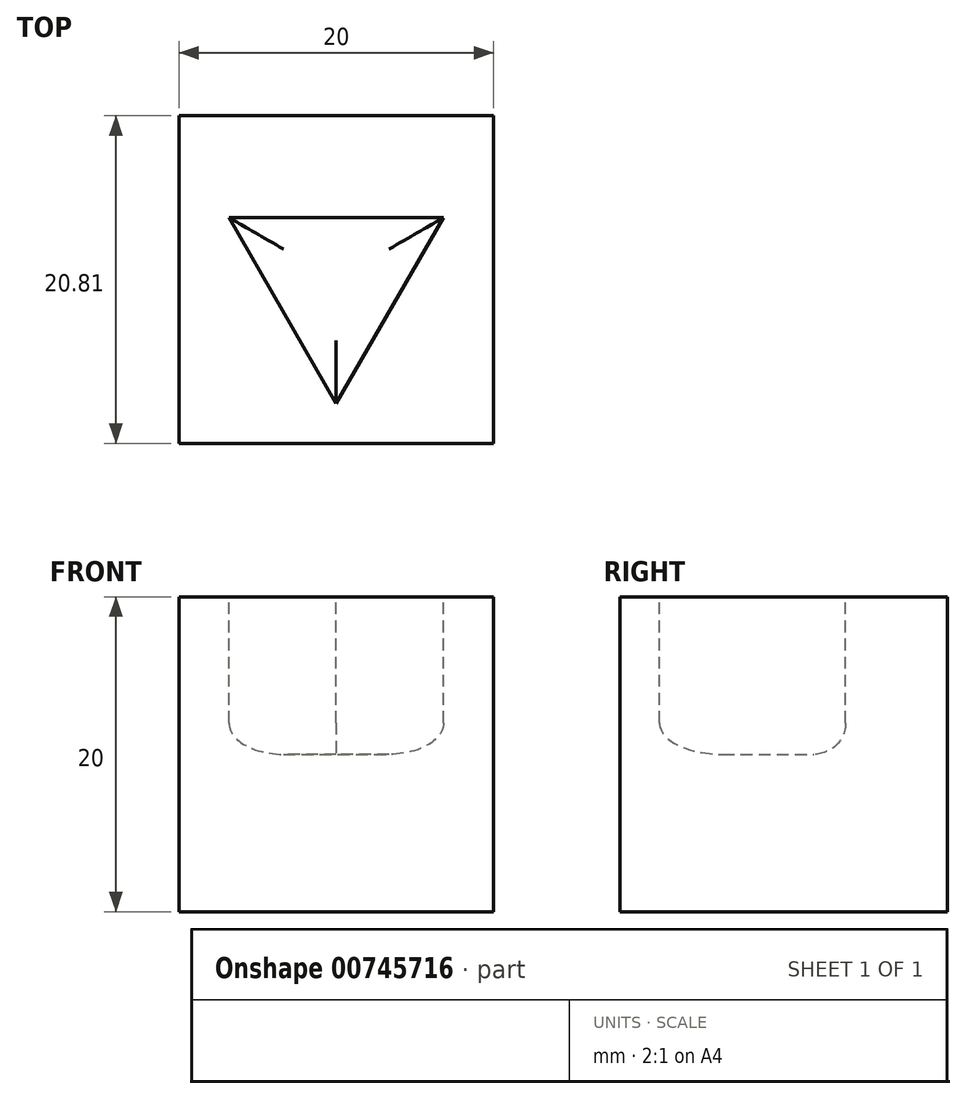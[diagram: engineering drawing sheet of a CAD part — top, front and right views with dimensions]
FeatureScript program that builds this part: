
annotation { "Feature Type Name" : "Feature", "Feature Type Description" : "" }
export const myFeature = defineFeature(function(context is Context, id is Id, definition is map)
    precondition{}
    {
        {
            var Q0;
            Q0=qCreatedBy(makeId("Front.planeOp"),FACE);
            var sketch = newSketch(context, id + "F0", { "sketchPlane" : qUnion([Q0])});
            skLineSegment(sketch, "E0", {"start": v(0, 0) * mm, "end": v(20, 0) * mm});
            skLineSegment(sketch, "E1", {"start": v(20, 0) * mm, "end": v(20, 20) * mm});
            skLineSegment(sketch, "E2", {"start": v(20, 20) * mm, "end": v(0, 20) * mm});
            skLineSegment(sketch, "E3", {"start": v(0, 20) * mm, "end": v(0, 0) * mm});
            skSolve(sketch);
        }
        {
            var Q0;
            Q0 = qSketchRegion(id + "F0", true);
            extrude(context, id + "F1", {"entities" : qUnion([Q0]), "depth" : 20.8 * mm, "offsetDistance" : 25.4 * mm});
        }
        {
            var Q0;
            Q0=makeQuery(id+"F1.opExtrude","SWEPT_FACE",FACE,{"disambiguationData":[OSD([sQuery(id+"F0.wireOp",EDGE,"E2")])]});
            var sketch = newSketch(context, id + "F2", { "sketchPlane" : qUnion([Q0])});
            skCircle(sketch, "E4.cCircle", {"center": v(10, -10.4) * mm, "radius": 7.88 * mm, "construction": true});
            skLineSegment(sketch, "E4.0", {"start": v(16.82, -6.47) * mm, "end": v(10, -18.28) * mm});
            skLineSegment(sketch, "E4.1", {"start": v(10, -18.28) * mm, "end": v(3.18, -6.47) * mm});
            skLineSegment(sketch, "E4.2", {"start": v(3.18, -6.47) * mm, "end": v(16.82, -6.47) * mm});
            skLineSegment(sketch, "E5", {"start": v(20, 0) * mm, "end": v(0, -20.8) * mm, "construction": true});
            skLineSegment(sketch, "E6", {"start": v(20, -20.8) * mm, "end": v(0, 0) * mm, "construction": true});
            skSolve(sketch);
        }
        {
            var Q0;
            Q0 = qSketchRegion(id + "F2", true);
            extrude(context, id + "F3", {"entities" : qUnion([Q0]), "operationType" : NewBodyOperationType.REMOVE, "oppositeDirection" : true, "depth" : 10 * mm, "offsetDistance" : 25.4 * mm});
        }
        {
            var Q0;
            Q0=makeQuery(id+"F3.boolean.opBoolean","COPY",EDGE,{"derivedFrom":makeQuery(id+"F3.opExtrude","CAP_EDGE",EDGE,{"disambiguationData":[OSD([sQuery(id+"F2.wireOp",EDGE,"E4.2")])],"isStart":false})});
            var Q1;
            Q1=makeQuery(id+"F3.boolean.opBoolean","COPY",EDGE,{"derivedFrom":makeQuery(id+"F3.opExtrude","CAP_EDGE",EDGE,{"disambiguationData":[OSD([sQuery(id+"F2.wireOp",EDGE,"E4.0")])],"isStart":false})});
            var Q2;
            Q2=makeQuery(id+"F3.boolean.opBoolean","COPY",EDGE,{"derivedFrom":makeQuery(id+"F3.opExtrude","CAP_EDGE",EDGE,{"disambiguationData":[OSD([sQuery(id+"F2.wireOp",EDGE,"E4.1")])],"isStart":false})});
            var Q3;
            Q3=makeQuery(id+"F3.boolean.opBoolean","COPY",EDGE,{"derivedFrom":makeQuery(id+"F3.opExtrude","CAP_EDGE",EDGE,{"disambiguationData":[OSD([sQuery(id+"F2.wireOp",EDGE,"E4.0")])],"isStart":true})});
            var Q4;
            Q4=makeQuery(id+"F3.boolean.opBoolean","COPY",EDGE,{"derivedFrom":makeQuery(id+"F3.opExtrude","CAP_EDGE",EDGE,{"disambiguationData":[OSD([sQuery(id+"F2.wireOp",EDGE,"E4.1")])],"isStart":true})});
            var Q5;
            Q5=makeQuery(id+"F3.boolean.opBoolean","COPY",EDGE,{"derivedFrom":makeQuery(id+"F3.opExtrude","CAP_EDGE",EDGE,{"disambiguationData":[OSD([sQuery(id+"F2.wireOp",EDGE,"E4.2")])],"isStart":true})});
            fillet(context, id + "F4", {"entities" : qUnion([Q0, Q1, Q2, Q3, Q4, Q5]), "radius" : 2 * mm, "allowEdgeOverflow" : false});
        }
    });
